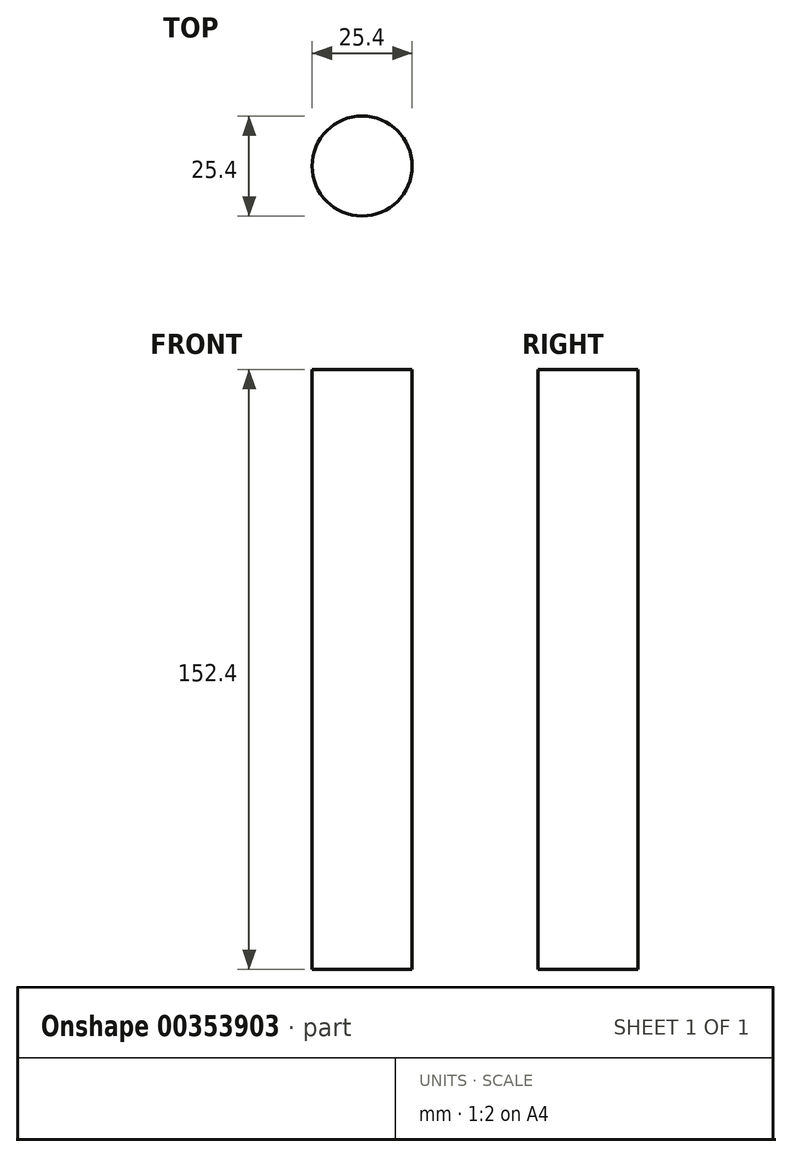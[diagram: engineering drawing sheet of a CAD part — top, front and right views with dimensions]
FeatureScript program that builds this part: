
annotation { "Feature Type Name" : "Feature", "Feature Type Description" : "" }
export const myFeature = defineFeature(function(context is Context, id is Id, definition is map)
    precondition{}
    {
        {
            var Q0;
            Q0=qCreatedBy(makeId("Top.planeOp"),FACE);
            var sketch = newSketch(context, id + "F0", { "sketchPlane" : qUnion([Q0])});
            skCircle(sketch, "E0", {"center": v(0, 0) * mm, "radius": 12.7 * mm});
            skSolve(sketch);
        }
        {
            var Q0;
            Q0=makeQuery(id+"F0.imprint","IMPRINT",FACE,{"disambiguationData":[TD([[makeQuery(id+"F0.imprint","IMPRINT",EDGE,{"derivedFrom":sQuery(id+"F0.wireOp",EDGE,"E0")}),1.0]])]});
            extrude(context, id + "F1", {"entities" : qUnion([Q0]), "depth" : 152.4 * mm});
        }
    });
